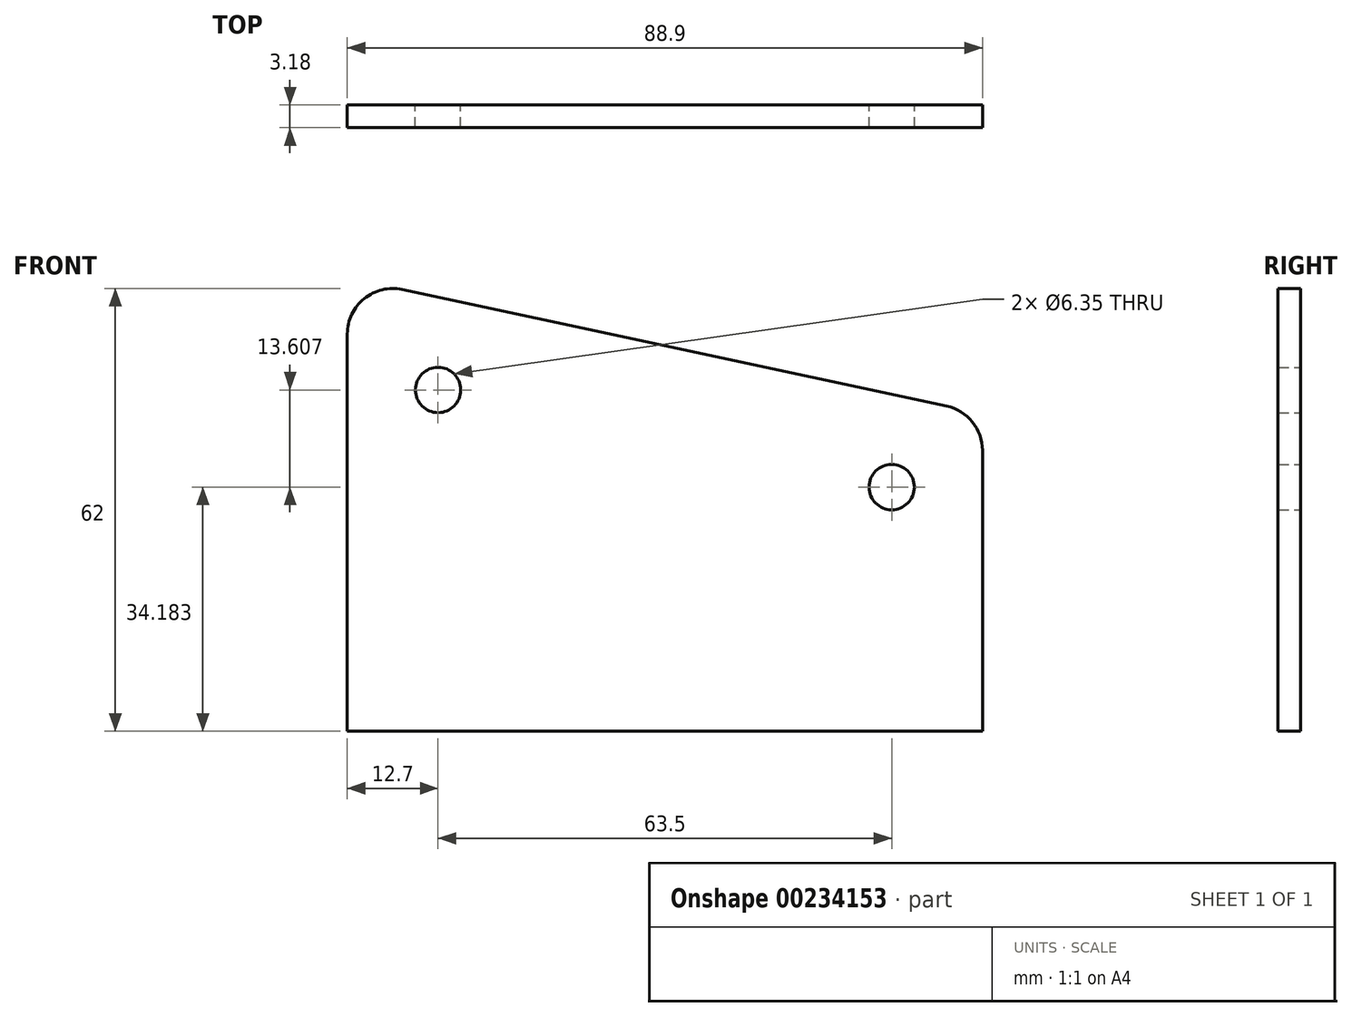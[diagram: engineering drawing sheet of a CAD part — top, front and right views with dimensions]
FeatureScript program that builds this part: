
annotation { "Feature Type Name" : "Feature", "Feature Type Description" : "" }
export const myFeature = defineFeature(function(context is Context, id is Id, definition is map)
    precondition{}
    {
        {
            var Q0;
            Q0=qCreatedBy(makeId("Front.planeOp"),FACE);
            var sketch = newSketch(context, id + "F0", { "sketchPlane" : qUnion([Q0])});
            skLineSegment(sketch, "E0", {"start": v(-44.45, 0) * mm, "end": v(-44.45, 55.65) * mm});
            skLineSegment(sketch, "E1", {"start": v(-36.77, 61.85) * mm, "end": v(39.43, 45.53) * mm});
            skLineSegment(sketch, "E2", {"start": v(44.45, 39.32) * mm, "end": v(44.45, 0) * mm});
            skLineSegment(sketch, "E3", {"start": v(44.45, 0) * mm, "end": v(-44.45, 0) * mm});
            skCircle(sketch, "E4", {"center": v(-31.75, 47.8) * mm, "radius": 3.18 * mm});
            skCircle(sketch, "E5", {"center": v(31.75, 34.18) * mm, "radius": 3.18 * mm});
            skPoint(sketch, "E6.visualSharp", {"position": v(44.45, 44.45) * mm});
            skArc(sketch, "E6.filletArc", {"start": v(44.45, 39.32) * mm, "mid": v(43.04, 43.3) * mm, "end": v(39.43, 45.53) * mm});
            skPoint(sketch, "E7.visualSharp", {"position": v(-44.45, 63.5) * mm});
            skArc(sketch, "E7.filletArc", {"start": v(-36.77, 61.85) * mm, "mid": v(-42.1, 60.58) * mm, "end": v(-44.45, 55.65) * mm});
            skSolve(sketch);
        }
        {
            var Q0;
            Q0=makeQuery(id+"F0.imprint","IMPRINT",FACE,{"disambiguationData":[TD([[makeQuery(id+"F0.imprint","IMPRINT",EDGE,{"derivedFrom":sQuery(id+"F0.wireOp",EDGE,"E0")}),-1.0]])]});
            extrude(context, id + "F1", {"entities" : qUnion([Q0]), "depth" : 3.17 * mm, "symmetric" : true});
        }
    });
